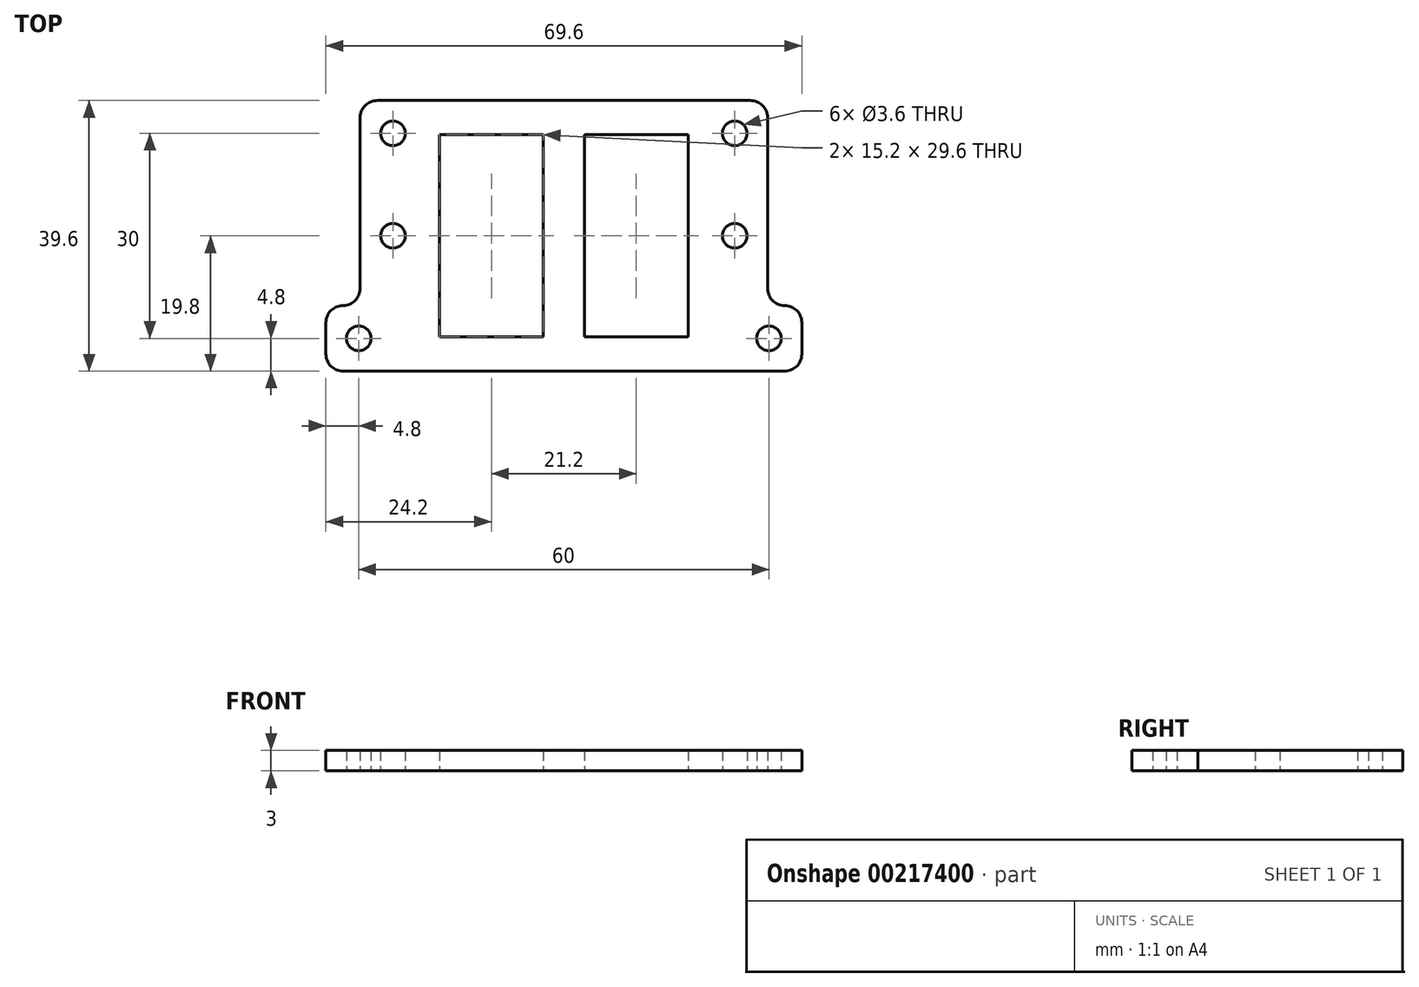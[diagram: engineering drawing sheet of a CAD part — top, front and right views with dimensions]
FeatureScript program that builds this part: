
annotation { "Feature Type Name" : "Feature", "Feature Type Description" : "" }
export const myFeature = defineFeature(function(context is Context, id is Id, definition is map)
    precondition{}
    {
        {
            var Q0;
            Q0=qCreatedBy(makeId("Top.planeOp"),FACE);
            var sketch = newSketch(context, id + "F0", { "sketchPlane" : qUnion([Q0])});
            skLineSegment(sketch, "E0.bottom", {"start": v(-34.8, 0) * mm, "end": v(34.8, 0) * mm});
            skLineSegment(sketch, "E0.top", {"start": v(-34.8, 9.6) * mm, "end": v(-29.8, 9.6) * mm});
            skLineSegment(sketch, "E0.left", {"start": v(-34.8, 0) * mm, "end": v(-34.8, 9.6) * mm});
            skLineSegment(sketch, "E0.right", {"start": v(34.8, 0) * mm, "end": v(34.8, 9.6) * mm});
            skLineSegment(sketch, "E1.top", {"start": v(-29.8, 39.6) * mm, "end": v(29.8, 39.6) * mm});
            skLineSegment(sketch, "E1.left", {"start": v(-29.8, 9.6) * mm, "end": v(-29.8, 39.6) * mm});
            skLineSegment(sketch, "E1.right", {"start": v(29.8, 9.6) * mm, "end": v(29.8, 39.6) * mm});
            skLineSegment(sketch, "E2.trimOffspring", {"start": v(29.8, 9.6) * mm, "end": v(34.8, 9.6) * mm});
            skLineSegment(sketch, "E3", {"start": v(0, 0) * mm, "end": v(0, 39.6) * mm, "construction": true});
            skLineSegment(sketch, "E4", {"start": v(-30, 4.8) * mm, "end": v(30, 4.8) * mm, "construction": true});
            skPoint(sketch, "E4.startSnap0", {"position": v(-34.8, 4.8) * mm});
            skPoint(sketch, "E4.endSnap0", {"position": v(34.8, 4.8) * mm});
            skPoint(sketch, "E5", {"position": v(0, 4.8) * mm});
            skCircle(sketch, "E6", {"center": v(-30, 4.8) * mm, "radius": 1.8 * mm});
            skCircle(sketch, "E7", {"center": v(30, 4.8) * mm, "radius": 1.8 * mm});
            skLineSegment(sketch, "E8", {"start": v(-25, 34.8) * mm, "end": v(25, 34.8) * mm, "construction": true});
            skPoint(sketch, "E9", {"position": v(0, 34.8) * mm});
            skCircle(sketch, "E10", {"center": v(-25, 34.8) * mm, "radius": 1.8 * mm});
            skCircle(sketch, "E11", {"center": v(25, 34.8) * mm, "radius": 1.8 * mm});
            skLineSegment(sketch, "E12.direction1", {"start": v(-25, 34.8) * mm, "end": v(0, 34.8) * mm, "construction": true});
            skCircle(sketch, "E13.0.1.0", {"center": v(-25, 19.8) * mm, "radius": 1.8 * mm});
            skCircle(sketch, "E13.0.1.1", {"center": v(25, 19.8) * mm, "radius": 1.8 * mm});
            skLineSegment(sketch, "E13.direction2", {"start": v(-25, 34.8) * mm, "end": v(-25, 19.8) * mm, "construction": true});
            skSolve(sketch);
        }
        {
            var Q0;
            Q0 = qSketchRegion(id + "F0", true);
            extrude(context, id + "F1", {"entities" : qUnion([Q0]), "depth" : 3 * mm});
        }
        {
            var Q0;
            Q0=makeQuery(id+"F1.opExtrude","SWEPT_EDGE",EDGE,{"disambiguationData":[OSD([sQuery(id+"F0.wireOp",EDGE,"E0.bottom"),sQuery(id+"F0.wireOp",EDGE,"E0.left")])]});
            var Q1;
            Q1=makeQuery(id+"F1.opExtrude","SWEPT_EDGE",EDGE,{"disambiguationData":[OSD([sQuery(id+"F0.wireOp",EDGE,"E0.top"),sQuery(id+"F0.wireOp",EDGE,"E0.left")])]});
            var Q2;
            Q2=makeQuery(id+"F1.opExtrude","SWEPT_EDGE",EDGE,{"disambiguationData":[OSD([sQuery(id+"F0.wireOp",EDGE,"E0.top"),sQuery(id+"F0.wireOp",EDGE,"E1.left")])]});
            var Q3;
            Q3=makeQuery(id+"F1.opExtrude","SWEPT_EDGE",EDGE,{"disambiguationData":[OSD([sQuery(id+"F0.wireOp",EDGE,"E0.bottom"),sQuery(id+"F0.wireOp",EDGE,"E0.right")])]});
            var Q4;
            Q4=makeQuery(id+"F1.opExtrude","SWEPT_EDGE",EDGE,{"disambiguationData":[OSD([sQuery(id+"F0.wireOp",EDGE,"E1.right"),sQuery(id+"F0.wireOp",EDGE,"E2.trimOffspring")])]});
            var Q5;
            Q5=makeQuery(id+"F1.opExtrude","SWEPT_EDGE",EDGE,{"disambiguationData":[OSD([sQuery(id+"F0.wireOp",EDGE,"E0.right"),sQuery(id+"F0.wireOp",EDGE,"E2.trimOffspring")])]});
            var Q6;
            Q6=makeQuery(id+"F1.opExtrude","SWEPT_EDGE",EDGE,{"disambiguationData":[OSD([sQuery(id+"F0.wireOp",EDGE,"E1.top"),sQuery(id+"F0.wireOp",EDGE,"E1.right")])]});
            var Q7;
            Q7=makeQuery(id+"F1.opExtrude","SWEPT_EDGE",EDGE,{"disambiguationData":[OSD([sQuery(id+"F0.wireOp",EDGE,"E1.top"),sQuery(id+"F0.wireOp",EDGE,"E1.left")])]});
            fillet(context, id + "F2", {"entities" : qUnion([Q0, Q1, Q2, Q3, Q4, Q5, Q6, Q7]), "radius" : 2.5 * mm, "tangentPropagation" : true, "allowEdgeOverflow" : false});
        }
        {
            var Q0;
            Q0=makeQuery(id+"F1.opExtrude","CAP_FACE",FACE,{"disambiguationData":[OSD([sQuery(id+"F0.wireOp",EDGE,"E0.bottom"),sQuery(id+"F0.wireOp",EDGE,"E0.top"),sQuery(id+"F0.wireOp",EDGE,"E0.left"),sQuery(id+"F0.wireOp",EDGE,"E0.right"),sQuery(id+"F0.wireOp",EDGE,"E1.top"),sQuery(id+"F0.wireOp",EDGE,"E1.left"),sQuery(id+"F0.wireOp",EDGE,"E1.right"),sQuery(id+"F0.wireOp",EDGE,"E2.trimOffspring"),sQuery(id+"F0.wireOp",EDGE,"E6"),sQuery(id+"F0.wireOp",EDGE,"E7"),sQuery(id+"F0.wireOp",EDGE,"E10"),sQuery(id+"F0.wireOp",EDGE,"E11"),sQuery(id+"F0.wireOp",EDGE,"E13.0.1.0"),sQuery(id+"F0.wireOp",EDGE,"E13.0.1.1")])],"isStart":true});
            var sketch = newSketch(context, id + "F3", { "sketchPlane" : qUnion([Q0])});
            skLineSegment(sketch, "E14", {"start": v(0, 0) * mm, "end": v(0, -39.6) * mm, "construction": true});
            skLineSegment(sketch, "E15.bottom", {"start": v(18.2, -34.6) * mm, "end": v(3, -34.6) * mm});
            skLineSegment(sketch, "E15.top", {"start": v(18.2, -5) * mm, "end": v(3, -5) * mm});
            skLineSegment(sketch, "E15.left", {"start": v(18.2, -34.6) * mm, "end": v(18.2, -5) * mm});
            skLineSegment(sketch, "E15.right", {"start": v(3, -34.6) * mm, "end": v(3, -5) * mm});
            skLineSegment(sketch, "E16.MirrorCS", {"start": v(-18.2, -34.6) * mm, "end": v(-3, -34.6) * mm});
            skLineSegment(sketch, "E17.MirrorCS", {"start": v(-3, -34.6) * mm, "end": v(-3, -5) * mm});
            skLineSegment(sketch, "E18.MirrorCS", {"start": v(-18.2, -5) * mm, "end": v(-3, -5) * mm});
            skLineSegment(sketch, "E19.MirrorCS", {"start": v(-18.2, -34.6) * mm, "end": v(-18.2, -5) * mm});
            skSolve(sketch);
        }
        {
            var Q0;
            Q0 = qSketchRegion(id + "F3", true);
            extrude(context, id + "F4", {"entities" : qUnion([Q0]), "operationType" : NewBodyOperationType.REMOVE, "endBound" : BoundingType.UP_TO_NEXT, "oppositeDirection" : true, "depth" : 25 * mm});
        }
    });
